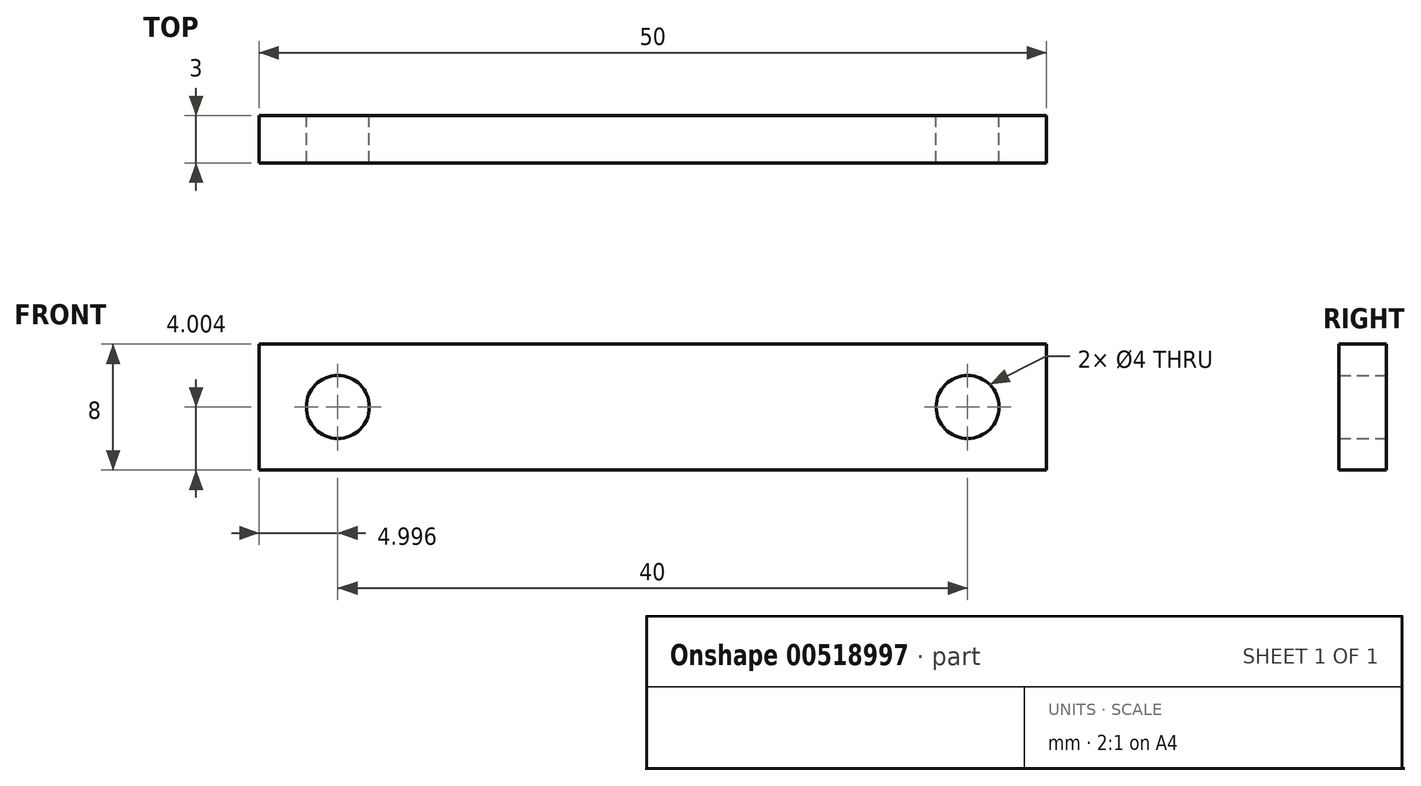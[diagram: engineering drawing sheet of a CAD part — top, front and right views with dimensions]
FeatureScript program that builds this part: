
annotation { "Feature Type Name" : "Feature", "Feature Type Description" : "" }
export const myFeature = defineFeature(function(context is Context, id is Id, definition is map)
    precondition{}
    {
        {
            var Q0;
            Q0=qCreatedBy(makeId("Front.planeOp"),FACE);
            var sketch = newSketch(context, id + "F0", { "sketchPlane" : qUnion([Q0])});
            skLineSegment(sketch, "E0.bottom", {"start": v(-25.44, 9.53) * mm, "end": v(24.56, 9.53) * mm});
            skLineSegment(sketch, "E0.top", {"start": v(-25.44, 1.53) * mm, "end": v(24.56, 1.53) * mm});
            skLineSegment(sketch, "E0.left", {"start": v(-25.44, 9.53) * mm, "end": v(-25.44, 1.53) * mm});
            skLineSegment(sketch, "E0.right", {"start": v(24.56, 9.53) * mm, "end": v(24.56, 1.53) * mm});
            skCircle(sketch, "E1", {"center": v(-20.44, 5.53) * mm, "radius": 2 * mm});
            skCircle(sketch, "E2", {"center": v(19.56, 5.53) * mm, "radius": 2 * mm});
            skSolve(sketch);
        }
        {
            var Q0;
            Q0=makeQuery(id+"F0.imprint","IMPRINT",FACE,{"disambiguationData":[TD([[makeQuery(id+"F0.imprint","IMPRINT",EDGE,{"derivedFrom":sQuery(id+"F0.wireOp",EDGE,"E0.bottom")}),-1.0]])]});
            extrude(context, id + "F1", {"entities" : qUnion([Q0]), "depth" : 3 * mm, "offsetDistance" : 25 * mm});
        }
    });
